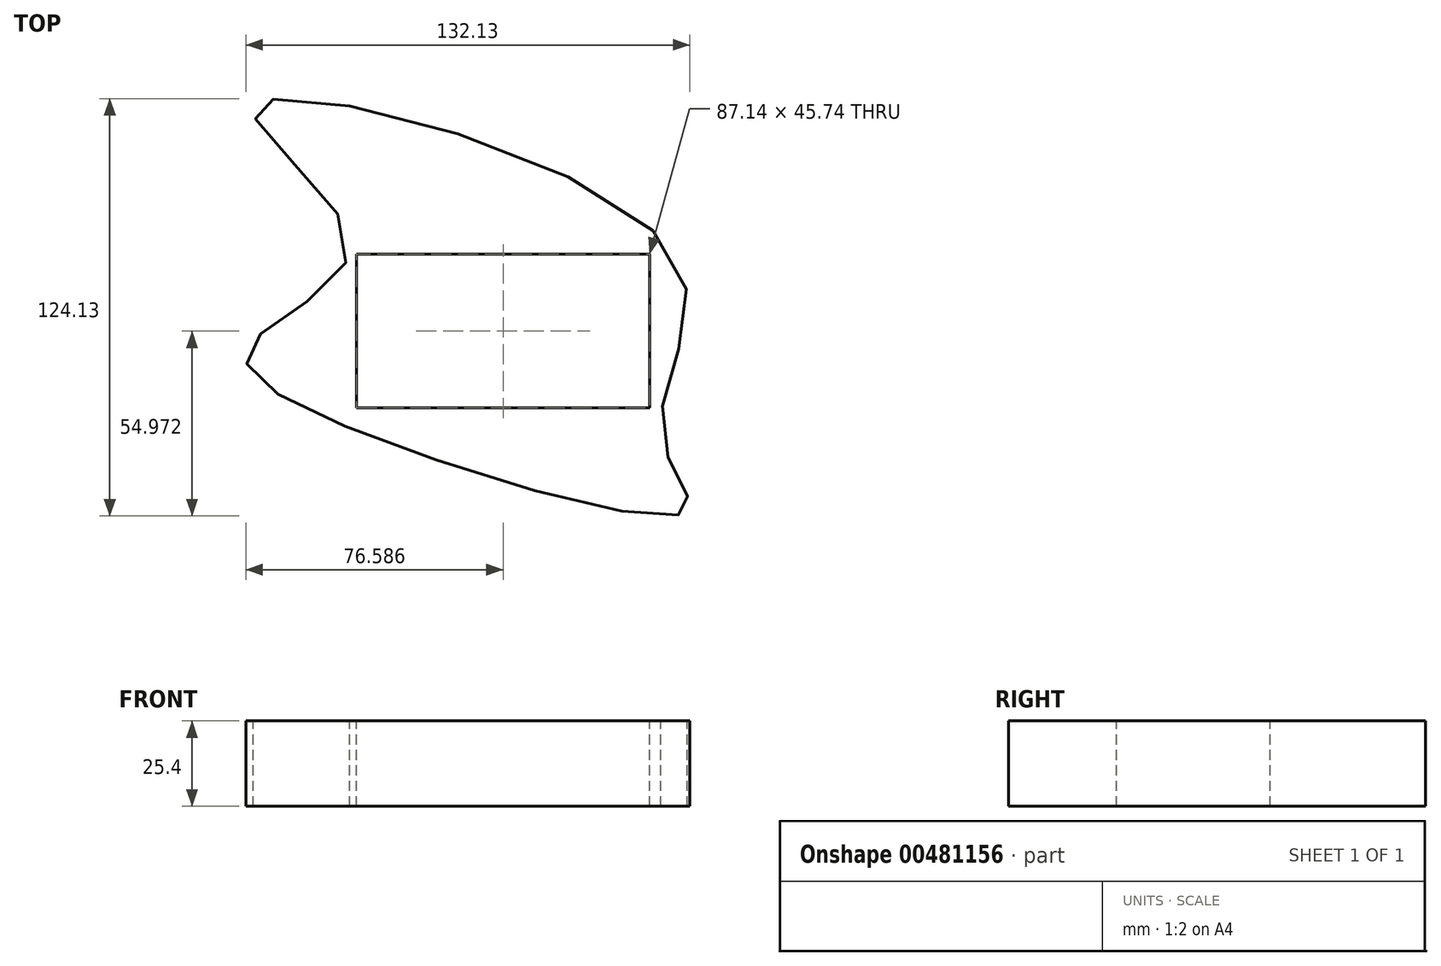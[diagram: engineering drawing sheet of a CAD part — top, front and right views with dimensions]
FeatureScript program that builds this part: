
annotation { "Feature Type Name" : "Feature", "Feature Type Description" : "" }
export const myFeature = defineFeature(function(context is Context, id is Id, definition is map)
    precondition{}
    {
        {
            var Q0;
            Q0=qCreatedBy(makeId("Top.planeOp"),FACE);
            var sketch = newSketch(context, id + "F0", { "sketchPlane" : qUnion([Q0])});
            skLineSegment(sketch, "E0.bottom", {"start": v(-53.84, -12.5) * mm, "end": v(33.3, -12.5) * mm});
            skLineSegment(sketch, "E0.top", {"start": v(-53.84, 33.23) * mm, "end": v(33.3, 33.23) * mm});
            skLineSegment(sketch, "E0.left", {"start": v(-53.84, -12.5) * mm, "end": v(-53.84, 33.23) * mm});
            skLineSegment(sketch, "E0.right", {"start": v(33.3, -12.5) * mm, "end": v(33.3, 33.23) * mm});
            skFitSpline(sketch, "E1", {"points": [v(-57.35, -17.92) * mm, v(44.72, -43.03) * mm, v(36.72, -19.45) * mm, v(39.25, 34.9) * mm, v(-84.33, 76.97) * mm, v(-55.95, 36.1) * mm, v(-85.74, 6) * mm, v(-57.35, -17.92) * mm]});
            skSolve(sketch);
        }
        {
            var Q0;
            Q0 = qSketchRegion(id + "F0", true);
            extrude(context, id + "F1", {"entities" : qUnion([Q0]), "oppositeDirection" : true, "depth" : 25.4 * mm});
        }
    });
